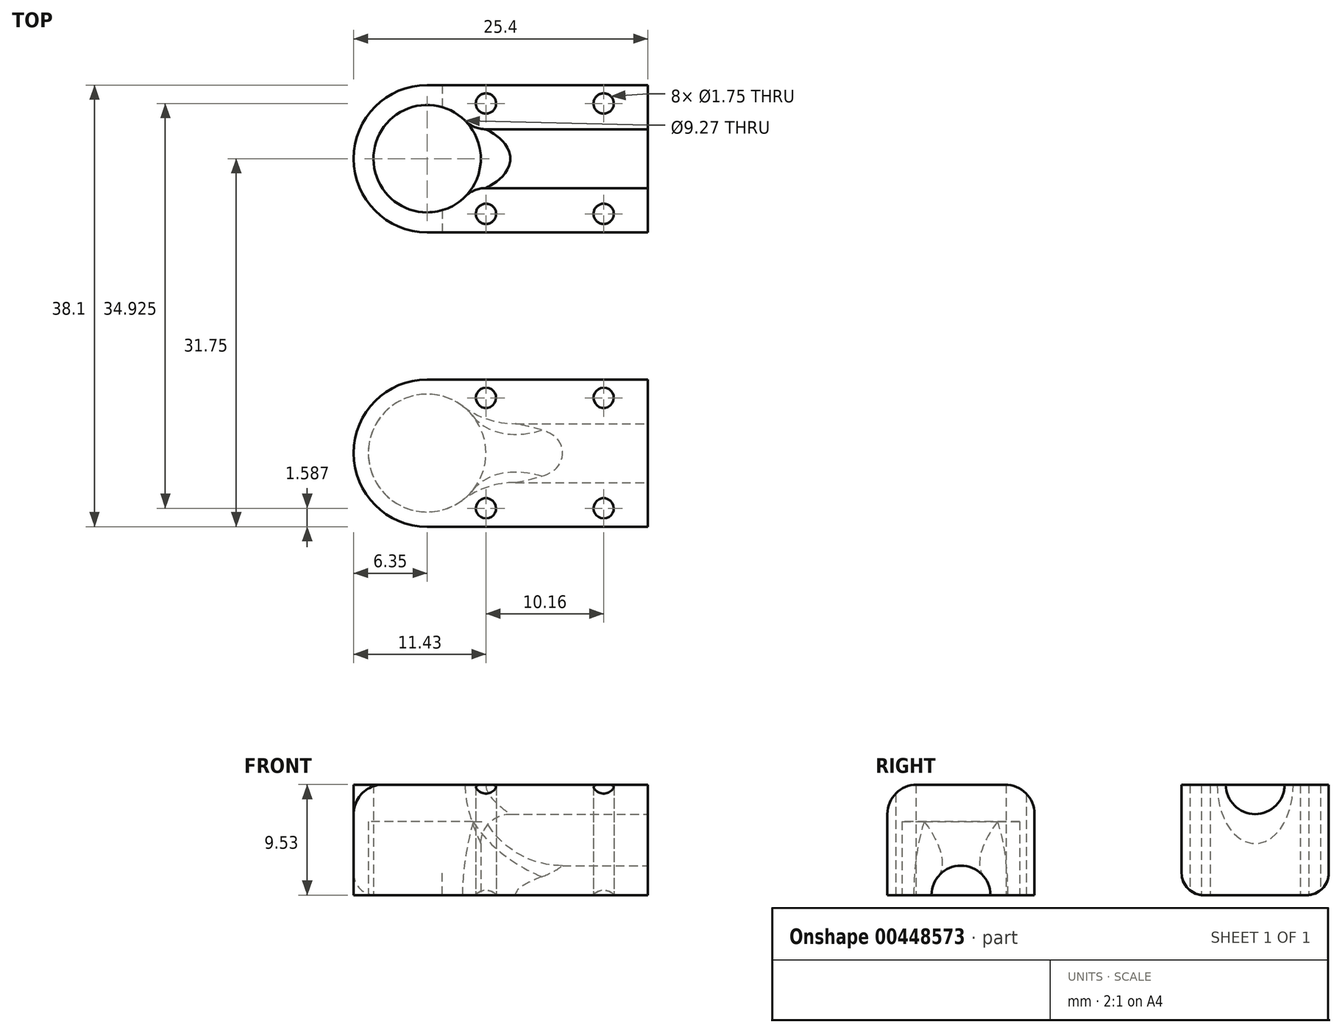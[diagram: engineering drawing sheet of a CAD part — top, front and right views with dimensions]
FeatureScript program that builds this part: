
annotation { "Feature Type Name" : "Feature", "Feature Type Description" : "" }
export const myFeature = defineFeature(function(context is Context, id is Id, definition is map)
    precondition{}
    {
        {
            var Q0;
            Q0=qCreatedBy(makeId("Top.planeOp"),FACE);
            var sketch = newSketch(context, id + "F0", { "sketchPlane" : qUnion([Q0])});
            skCircle(sketch, "E0", {"center": v(0, 0) * mm, "radius": 4.64 * mm});
            skArc(sketch, "E1", {"start": v(0, 6.35) * mm, "mid": v(-6.35, 0) * mm, "end": v(0, -6.35) * mm});
            skLineSegment(sketch, "E2.bottom", {"start": v(0, 6.35) * mm, "end": v(19.05, 6.35) * mm});
            skLineSegment(sketch, "E2.top", {"start": v(0, -6.35) * mm, "end": v(19.05, -6.35) * mm});
            skLineSegment(sketch, "E2.right", {"start": v(19.05, 6.35) * mm, "end": v(19.05, -6.35) * mm});
            skPoint(sketch, "E3", {"position": v(15.24, -4.76) * mm});
            skPoint(sketch, "E4", {"position": v(5.08, -4.76) * mm});
            skPoint(sketch, "E5", {"position": v(5.08, 4.76) * mm});
            skPoint(sketch, "E6", {"position": v(15.24, 4.76) * mm});
            skSolve(sketch);
        }
        {
            var Q0;
            Q0=makeQuery(id+"F0.imprint","IMPRINT",FACE,{"disambiguationData":[TD([[makeQuery(id+"F0.imprint","IMPRINT",EDGE,{"derivedFrom":sQuery(id+"F0.wireOp",EDGE,"E0")}),-1.0]])]});
            extrude(context, id + "F1", {"entities" : qUnion([Q0]), "depth" : 9.52 * mm, "offsetDistance" : 25.4 * mm});
        }
        {
            var Q0;
            Q0=makeQuery(id+"F1.opExtrude","SWEPT_FACE",FACE,{"disambiguationData":[OSD([sQuery(id+"F0.wireOp",EDGE,"E2.right")])]});
            var sketch = newSketch(context, id + "F2", { "sketchPlane" : qUnion([Q0])});
            skCircle(sketch, "E7", {"center": v(0, 9.53) * mm, "radius": 2.54 * mm});
            skSolve(sketch);
        }
        {
            var Q0;
            {var subQ0=sQuery(id+"F2.wireOp",EDGE,"E7");var subQ1=makeQuery(id+"F1.opExtrude","CAP_EDGE",EDGE,{"disambiguationData":[OSD([sQuery(id+"F0.wireOp",EDGE,"E2.right")])],"isStart":false});var subQ2=makeQuery(id+"F2.imprint","INTERSECT",VERTEX,{"disambiguationData":[OD(0.0)],"derivedFrom":[subQ1,subQ0]});Q0=makeQuery(id+"F2.imprint","IMPRINT",FACE,{"disambiguationData":[TD([[makeQuery(id+"F2.imprint","IMPRINT",EDGE,{"disambiguationData":[TD([[subQ2,-1.0]])],"derivedFrom":subQ0}),1.0]])]});}
            var Q1;
            {var subQ0=sQuery(id+"F2.wireOp",EDGE,"E7");var subQ1=makeQuery(id+"F1.opExtrude","CAP_EDGE",EDGE,{"disambiguationData":[OSD([sQuery(id+"F0.wireOp",EDGE,"E2.right")])],"isStart":false});var subQ2=makeQuery(id+"F2.imprint","INTERSECT",VERTEX,{"disambiguationData":[OD(0.0)],"derivedFrom":[subQ1,subQ0]});Q1=makeQuery(id+"F2.imprint","IMPRINT",FACE,{"disambiguationData":[TD([[makeQuery(id+"F2.imprint","IMPRINT",EDGE,{"disambiguationData":[TD([[subQ2,1.0]])],"derivedFrom":subQ0}),1.0]])]});}
            extrude(context, id + "F3", {"entities" : qUnion([Q0, Q1]), "operationType" : NewBodyOperationType.REMOVE, "oppositeDirection" : true, "depth" : 15.4 * mm, "offsetDistance" : 25.4 * mm});
        }
        {
            var Q0;
            Q0=makeQuery(id+"F3.boolean.opBoolean","INTERSECT",EDGE,{"derivedFrom":[makeQuery(id+"F1.opExtrude","SWEPT_FACE",FACE,{"disambiguationData":[OSD([sQuery(id+"F0.wireOp",EDGE,"E0")])]}),makeQuery(id+"F3.opExtrude","SWEPT_FACE",FACE,{"disambiguationData":[OSD([sQuery(id+"F2.wireOp",EDGE,"E7")])]})]});
            fillet(context, id + "F4", {"entities" : qUnion([Q0]), "radius" : 2.54 * mm, "tangentPropagation" : true, "allowEdgeOverflow" : false});
        }
        {
            var Q0;
            Q0=sQuery(id+"F0.wireOp",VERTEX,"E4");
            var Q1;
            Q1=sQuery(id+"F0.wireOp",VERTEX,"E3");
            var Q2;
            Q2=sQuery(id+"F0.wireOp",VERTEX,"E6");
            var Q3;
            Q3=sQuery(id+"F0.wireOp",VERTEX,"E5");
            var Q4;
            Q4=makeQuery(id+"F1.opExtrude","SWEPT_BODY",BODY,{"disambiguationData":[OSD([sQuery(id+"F0.wireOp",EDGE,"E0"),sQuery(id+"F0.wireOp",EDGE,"E1"),sQuery(id+"F0.wireOp",EDGE,"E2.bottom"),sQuery(id+"F0.wireOp",EDGE,"E2.top"),sQuery(id+"F0.wireOp",EDGE,"E2.right")])]});
            hole(context, id + "F5", {"style" : HoleStyle.SIMPLE, "endStyle" : HoleEndStyle.THROUGH, "oppositeDirection" : true, "holeDiameter" : 1.75 * mm, "majorDiameter" : 6.35 * mm, "isTappedThrough" : true, "tappedDepth" : 12.7 * mm, "tapClearance" : 3, "startFromSketch" : true, "locations" : qUnion([Q0, Q1, Q2, Q3]), "scope" : qUnion([Q4])});
        }
        {
            var Q0;
            Q0=makeQuery(id+"F1.opExtrude","CAP_EDGE",EDGE,{"disambiguationData":[OSD([sQuery(id+"F0.wireOp",EDGE,"E2.top")])],"isStart":true});
            fillet(context, id + "F6", {"entities" : qUnion([Q0]), "radius" : 1.9 * mm, "tangentPropagation" : true, "allowEdgeOverflow" : false});
        }
        {
            var Q0;
            Q0=qCreatedBy(makeId("Top.planeOp"),FACE);
            var sketch = newSketch(context, id + "F7", { "sketchPlane" : qUnion([Q0])});
            skCircle(sketch, "E8", {"center": v(0, -25.4) * mm, "radius": 5.08 * mm});
            skArc(sketch, "E9", {"start": v(0, -19.05) * mm, "mid": v(-6.35, -25.4) * mm, "end": v(0, -31.75) * mm});
            skLineSegment(sketch, "E10.bottom", {"start": v(0, -31.75) * mm, "end": v(19.05, -31.75) * mm});
            skLineSegment(sketch, "E10.top", {"start": v(0, -19.05) * mm, "end": v(19.05, -19.05) * mm});
            skLineSegment(sketch, "E10.right", {"start": v(19.05, -31.75) * mm, "end": v(19.05, -19.05) * mm});
            skPoint(sketch, "E11", {"position": v(5.08, -30.16) * mm});
            skPoint(sketch, "E12", {"position": v(15.24, -30.16) * mm});
            skPoint(sketch, "E13", {"position": v(15.24, -20.64) * mm});
            skPoint(sketch, "E14", {"position": v(5.08, -20.64) * mm});
            skLineSegment(sketch, "E15", {"start": v(0, -25.4) * mm, "end": v(22.13, -25.4) * mm, "construction": true});
            skSolve(sketch);
        }
        {
            var Q0;
            Q0=makeQuery(id+"F7.imprint","IMPRINT",FACE,{"disambiguationData":[TD([[makeQuery(id+"F7.imprint","IMPRINT",EDGE,{"derivedFrom":sQuery(id+"F7.wireOp",EDGE,"E8")}),-1.0]])]});
            var Q1;
            Q1=makeQuery(id+"F7.imprint","IMPRINT",FACE,{"disambiguationData":[TD([[makeQuery(id+"F7.imprint","IMPRINT",EDGE,{"derivedFrom":sQuery(id+"F7.wireOp",EDGE,"E8")}),1.0]])]});
            extrude(context, id + "F8", {"entities" : qUnion([Q0, Q1]), "depth" : 9.52 * mm, "offsetDistance" : 25.4 * mm});
        }
        {
            var Q0;
            Q0=makeQuery(id+"F7.imprint","IMPRINT",FACE,{"disambiguationData":[TD([[makeQuery(id+"F7.imprint","IMPRINT",EDGE,{"derivedFrom":sQuery(id+"F7.wireOp",EDGE,"E8")}),1.0]])]});
            extrude(context, id + "F9", {"entities" : qUnion([Q0]), "operationType" : NewBodyOperationType.REMOVE, "depth" : 6.35 * mm, "offsetDistance" : 25.4 * mm});
        }
        {
            var Q0;
            Q0=makeQuery(id+"F8.opExtrude","SWEPT_FACE",FACE,{"disambiguationData":[OSD([sQuery(id+"F7.wireOp",EDGE,"E10.right")])]});
            var sketch = newSketch(context, id + "F10", { "sketchPlane" : qUnion([Q0])});
            skCircle(sketch, "E16", {"center": v(-25.4, 0) * mm, "radius": 2.54 * mm});
            skSolve(sketch);
        }
        {
            var Q0;
            {var subQ0=sQuery(id+"F10.wireOp",EDGE,"E16");var subQ1=makeQuery(id+"F8.opExtrude","CAP_EDGE",EDGE,{"disambiguationData":[OSD([sQuery(id+"F7.wireOp",EDGE,"E10.right")])],"isStart":true});var subQ2=makeQuery(id+"F10.imprint","INTERSECT",VERTEX,{"disambiguationData":[OD(0.0)],"derivedFrom":[subQ1,subQ0]});Q0=makeQuery(id+"F10.imprint","IMPRINT",FACE,{"disambiguationData":[TD([[makeQuery(id+"F10.imprint","IMPRINT",EDGE,{"disambiguationData":[TD([[subQ2,-1.0]])],"derivedFrom":subQ0}),1.0]])]});}
            var Q1;
            {var subQ0=sQuery(id+"F10.wireOp",EDGE,"E16");var subQ1=makeQuery(id+"F8.opExtrude","CAP_EDGE",EDGE,{"disambiguationData":[OSD([sQuery(id+"F7.wireOp",EDGE,"E10.right")])],"isStart":true});var subQ2=makeQuery(id+"F10.imprint","INTERSECT",VERTEX,{"disambiguationData":[OD(0.0)],"derivedFrom":[subQ1,subQ0]});Q1=makeQuery(id+"F10.imprint","IMPRINT",FACE,{"disambiguationData":[TD([[makeQuery(id+"F10.imprint","IMPRINT",EDGE,{"disambiguationData":[TD([[subQ2,1.0]])],"derivedFrom":subQ0}),1.0]])]});}
            extrude(context, id + "F11", {"entities" : qUnion([Q0, Q1]), "operationType" : NewBodyOperationType.REMOVE, "oppositeDirection" : true, "depth" : 15.4 * mm, "offsetDistance" : 25.4 * mm});
        }
        {
            var Q0;
            Q0=makeQuery(id+"F8.opExtrude","CAP_EDGE",EDGE,{"disambiguationData":[OSD([sQuery(id+"F7.wireOp",EDGE,"E10.bottom")])],"isStart":false});
            fillet(context, id + "F12", {"entities" : qUnion([Q0]), "radius" : 2.54 * mm, "tangentPropagation" : true, "allowEdgeOverflow" : false});
        }
        {
            var Q0;
            Q0=sQuery(id+"F7.wireOp",VERTEX,"E11");
            var Q1;
            Q1=sQuery(id+"F7.wireOp",VERTEX,"E12");
            var Q2;
            Q2=sQuery(id+"F7.wireOp",VERTEX,"E13");
            var Q3;
            Q3=sQuery(id+"F7.wireOp",VERTEX,"E14");
            var Q4;
            Q4=makeQuery(id+"F8.opExtrude","SWEPT_BODY",BODY,{"disambiguationData":[OSD([sQuery(id+"F7.wireOp",EDGE,"E9"),sQuery(id+"F7.wireOp",EDGE,"E10.bottom"),sQuery(id+"F7.wireOp",EDGE,"E10.top"),sQuery(id+"F7.wireOp",EDGE,"E10.right")])]});
            hole(context, id + "F13", {"style" : HoleStyle.SIMPLE, "endStyle" : HoleEndStyle.THROUGH, "oppositeDirection" : true, "holeDiameter" : 1.75 * mm, "majorDiameter" : 6.35 * mm, "isTappedThrough" : true, "tappedDepth" : 12.7 * mm, "tapClearance" : 3, "startFromSketch" : true, "locations" : qUnion([Q0, Q1, Q2, Q3]), "scope" : qUnion([Q4])});
        }
        {
            var Q0;
            Q0=makeQuery(id+"F11.boolean.opBoolean","INTERSECT",EDGE,{"derivedFrom":[makeQuery(id+"F9.boolean.opBoolean","COPY",FACE,{"derivedFrom":makeQuery(id+"F9.opExtrude","SWEPT_FACE",FACE,{"disambiguationData":[OSD([sQuery(id+"F7.wireOp",EDGE,"E8")])]})}),makeQuery(id+"F11.opExtrude","SWEPT_FACE",FACE,{"disambiguationData":[OSD([sQuery(id+"F10.wireOp",EDGE,"E16")])]})]});
            fillet(context, id + "F14", {"entities" : qUnion([Q0]), "radius" : 7.62 * mm, "tangentPropagation" : true, "allowEdgeOverflow" : false});
        }
    });
